# Revit family: WH3378-HC-PPZ
name_source: partatom
category: Plumbing Fixtures
revit_build: Autodesk Revit MEP 2016 (Build: 20150220_1215(x64)
units: mm (PartAtom-declared; Revit-internal decimal feet)

## family parameters
Cut with Voids When Loaded = No
Host = Face
OmniClass Number = 23.45.55.17
OmniClass Title = Mixing Faucets
Part Type = Normal
Room Calculation Point = No
Round Connector Dimension = Use Diameter
Shared = Yes

## types (1)
- WH3378-HC-PPZ
    Amperage = 0
    CW Connection = Yes
    Default Elevation = 0"
    Description = Ligature Resistant Dual Temperature, Piezo Button Faucet with 4" Centerset
    HW Connection = Yes
    Manufacturer = Whitehall
    Material = Type 304 Stainless Steel
    Model = WH3378-HC-PPZ
    Revised Date = 10/01/19
    Tempered Water Connection = No
    URL = http://www.whitehallmfg.com
    Vent Connection = No
    Voltage = 0
    WH3378-HC-PPZ - Ligature Resistant Dual Temperature, Piezo Button Faucet with 4" Centerset = Yes
    Waste Connection = No

## geometry (parser evidence)
native form markers: Sweep x6
no freeform markers — native parametric forms only
